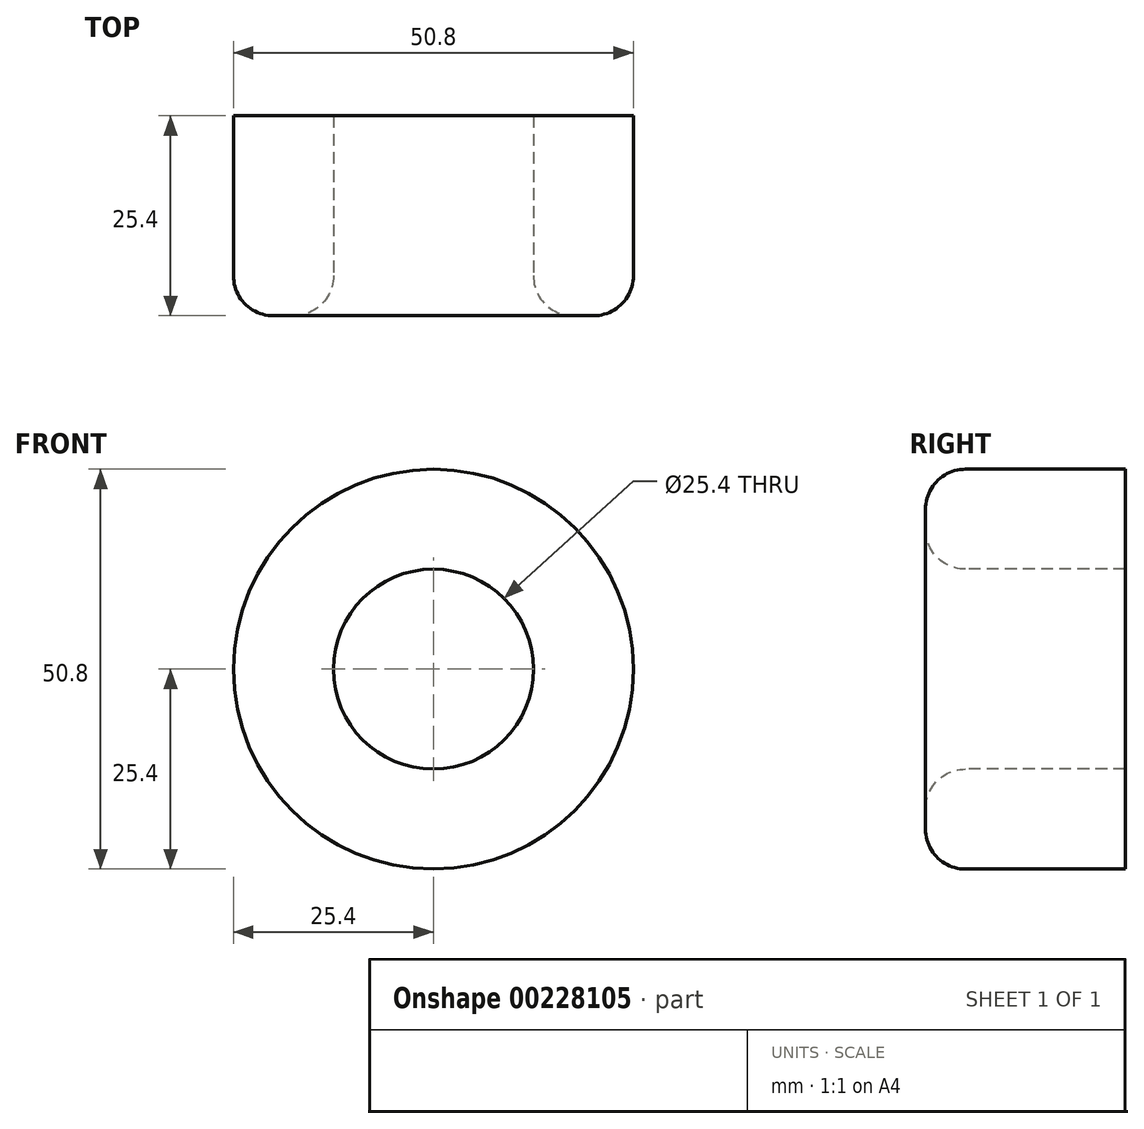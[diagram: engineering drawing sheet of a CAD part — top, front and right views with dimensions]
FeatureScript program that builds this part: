
annotation { "Feature Type Name" : "Feature", "Feature Type Description" : "" }
export const myFeature = defineFeature(function(context is Context, id is Id, definition is map)
    precondition{}
    {
        {
            var Q0;
            Q0=qCreatedBy(makeId("Front.planeOp"),FACE);
            var sketch = newSketch(context, id + "F0", { "sketchPlane" : qUnion([Q0])});
            skCircle(sketch, "E0", {"center": v(0, 0) * mm, "radius": 25.4 * mm});
            skSolve(sketch);
        }
        {
            var Q0;
            Q0=makeQuery(id+"F0.imprint","IMPRINT",FACE,{"disambiguationData":[TD([[makeQuery(id+"F0.imprint","IMPRINT",EDGE,{"derivedFrom":sQuery(id+"F0.wireOp",EDGE,"E0")}),1.0]])]});
            extrude(context, id + "F1", {"entities" : qUnion([Q0]), "depth" : 25.4 * mm});
        }
        {
            var Q0;
            Q0=makeQuery(id+"F1.opExtrude","CAP_FACE",FACE,{"disambiguationData":[OSD([sQuery(id+"F0.wireOp",EDGE,"E0")])],"isStart":false});
            var sketch = newSketch(context, id + "F2", { "sketchPlane" : qUnion([Q0])});
            skCircle(sketch, "E1", {"center": v(0, 0) * mm, "radius": 12.7 * mm});
            skSolve(sketch);
        }
        {
            var Q0;
            Q0 = qSketchRegion(id + "F2", true);
            extrude(context, id + "F3", {"entities" : qUnion([Q0]), "operationType" : NewBodyOperationType.REMOVE, "endBound" : BoundingType.THROUGH_ALL, "oppositeDirection" : true, "depth" : 25.4 * mm});
        }
        {
            var Q0;
            Q0=makeQuery(id+"F1.opExtrude","CAP_FACE",FACE,{"disambiguationData":[OSD([sQuery(id+"F0.wireOp",EDGE,"E0")])],"isStart":false});
            fillet(context, id + "F4", {"entities" : qUnion([Q0]), "radius" : 5.08 * mm, "tangentPropagation" : true, "allowEdgeOverflow" : false});
        }
    });
